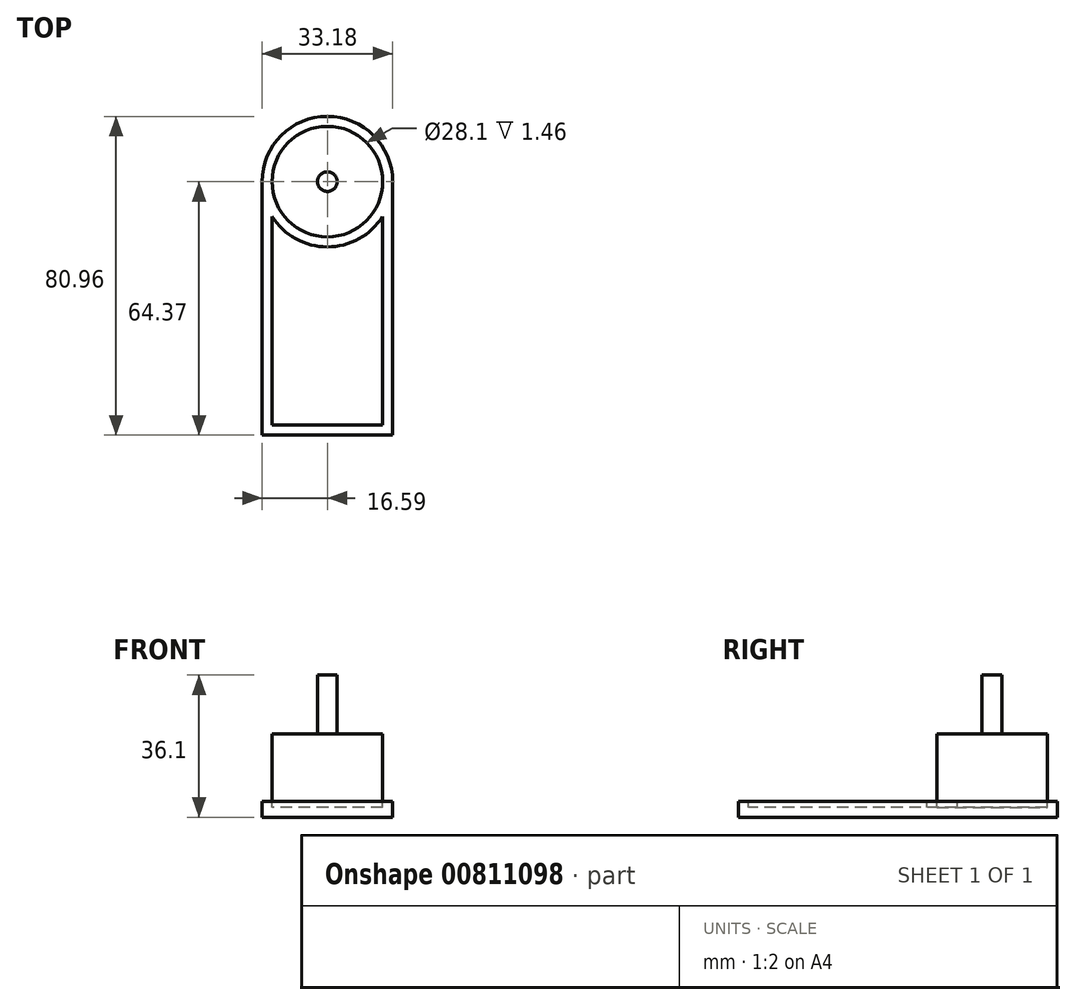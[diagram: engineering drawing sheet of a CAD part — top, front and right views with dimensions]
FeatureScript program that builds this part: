
annotation { "Feature Type Name" : "Feature", "Feature Type Description" : "" }
export const myFeature = defineFeature(function(context is Context, id is Id, definition is map)
    precondition{}
    {
        {
            var Q0;
            Q0=qCreatedBy(makeId("Top.planeOp"),FACE);
            var sketch = newSketch(context, id + "F0", { "sketchPlane" : qUnion([Q0])});
            skCircle(sketch, "E0", {"center": v(0, 0) * mm, "radius": 14.05 * mm});
            skSolve(sketch);
        }
        {
            var Q0;
            Q0=makeQuery(id+"F0.imprint","IMPRINT",FACE,{"disambiguationData":[TD([[makeQuery(id+"F0.imprint","IMPRINT",EDGE,{"derivedFrom":sQuery(id+"F0.wireOp",EDGE,"E0")}),1.0]])]});
            extrude(context, id + "F1", {"entities" : qUnion([Q0]), "depth" : 17.1 * mm, "offsetDistance" : 25.4 * mm});
        }
        {
            var Q0;
            Q0=makeQuery(id+"F1.opExtrude","CAP_FACE",FACE,{"disambiguationData":[OSD([sQuery(id+"F0.wireOp",EDGE,"E0")])],"isStart":false});
            var sketch = newSketch(context, id + "F2", { "sketchPlane" : qUnion([Q0])});
            skCircle(sketch, "E1", {"center": v(0, 0) * mm, "radius": 2.5 * mm});
            skSolve(sketch);
        }
        {
            var Q0;
            Q0=makeQuery(id+"F2.imprint","IMPRINT",FACE,{"disambiguationData":[TD([[makeQuery(id+"F2.imprint","IMPRINT",EDGE,{"derivedFrom":sQuery(id+"F2.wireOp",EDGE,"E1")}),1.0]])]});
            extrude(context, id + "F3", {"entities" : qUnion([Q0]), "operationType" : NewBodyOperationType.ADD, "depth" : 15 * mm, "offsetDistance" : 25.4 * mm});
        }
        {
            var Q0;
            Q0=makeQuery(id+"F1.opExtrude","CAP_FACE",FACE,{"disambiguationData":[OSD([sQuery(id+"F0.wireOp",EDGE,"E0")])],"isStart":true});
            var sketch = newSketch(context, id + "F4", { "sketchPlane" : qUnion([Q0])});
            skCircle(sketch, "E2.0", {"center": v(0, 0) * mm, "radius": 14.05 * mm, "construction": true});
            skCircle(sketch, "E3.0", {"center": v(0, 0) * mm, "radius": 16.59 * mm});
            skLineSegment(sketch, "E4.bottom", {"start": v(16.59, 0) * mm, "end": v(0, 0) * mm});
            skLineSegment(sketch, "E4.top", {"start": v(16.6, 64.37) * mm, "end": v(0, 64.37) * mm});
            skLineSegment(sketch, "E4.left", {"start": v(16.6, 0) * mm, "end": v(16.59, 64.37) * mm});
            skLineSegment(sketch, "E4.right", {"start": v(0, 0) * mm, "end": v(0, 64.37) * mm, "construction": true});
            skLineSegment(sketch, "E5.bottom", {"start": v(-16.59, 0) * mm, "end": v(0, 0) * mm});
            skLineSegment(sketch, "E5.top", {"start": v(-16.6, 64.37) * mm, "end": v(0, 64.37) * mm});
            skLineSegment(sketch, "E5.left", {"start": v(-16.59, 0) * mm, "end": v(-16.6, 64.37) * mm});
            skSolve(sketch);
        }
        {
            var Q0;
            Q0=makeQuery(id+"F4.imprint","IMPRINT",FACE,{"disambiguationData":[TD([[makeQuery(id+"F4.imprint","IMPRINT",EDGE,{"derivedFrom":sQuery(id+"F4.wireOp",EDGE,"E4.top")}),1.0]])]});
            var Q1;
            {var subQ0=sQuery(id+"F4.wireOp",EDGE,"E4.bottom");var subQ5=makeQuery(id+"F1.opExtrude","CAP_EDGE",EDGE,{"disambiguationData":[OSD([sQuery(id+"F0.wireOp",EDGE,"E0")])],"isStart":true});var subQ7=makeQuery(id+"F4.imprint","INTERSECT",VERTEX,{"derivedFrom":[subQ5,subQ0]});Q1=makeQuery(id+"F4.imprint","IMPRINT",FACE,{"disambiguationData":[TD([[makeQuery(id+"F4.imprint","IMPRINT",EDGE,{"disambiguationData":[TD([[subQ7,-1.0]])],"derivedFrom":subQ5}),1.0]])]});}
            var Q2;
            {var subQ0=sQuery(id+"F4.wireOp",EDGE,"E4.bottom");var subQ5=makeQuery(id+"F1.opExtrude","CAP_EDGE",EDGE,{"disambiguationData":[OSD([sQuery(id+"F0.wireOp",EDGE,"E0")])],"isStart":true});var subQ6=makeQuery(id+"F4.imprint","INTERSECT",VERTEX,{"derivedFrom":[subQ5,subQ0]});Q2=makeQuery(id+"F4.imprint","IMPRINT",FACE,{"disambiguationData":[TD([[makeQuery(id+"F4.imprint","IMPRINT",EDGE,{"disambiguationData":[TD([[subQ6,1.0]])],"derivedFrom":subQ5}),1.0]])]});}
            var Q3;
            {var subQ0=sQuery(id+"F4.wireOp",EDGE,"E5.bottom");var subQ1=sQuery(id+"F4.wireOp",EDGE,"E4.bottom");var subQ2=makeQuery(id+"F4.imprint","INTERSECT",VERTEX,{"derivedFrom":[subQ1,subQ0]});Q3=makeQuery(id+"F4.imprint","IMPRINT",FACE,{"disambiguationData":[TD([[makeQuery(id+"F4.imprint","IMPRINT",EDGE,{"disambiguationData":[TD([[subQ2,1.0]])],"derivedFrom":subQ1}),1.0]])]});}
            var Q4;
            {var subQ0=sQuery(id+"F4.wireOp",EDGE,"E5.bottom");var subQ1=sQuery(id+"F4.wireOp",EDGE,"E4.bottom");var subQ2=makeQuery(id+"F4.imprint","INTERSECT",VERTEX,{"derivedFrom":[subQ1,subQ0]});Q4=makeQuery(id+"F4.imprint","IMPRINT",FACE,{"disambiguationData":[TD([[makeQuery(id+"F4.imprint","IMPRINT",EDGE,{"disambiguationData":[TD([[subQ2,1.0]])],"derivedFrom":subQ1}),-1.0]])]});}
            extrude(context, id + "F5", {"entities" : qUnion([Q0, Q1, Q2, Q3, Q4]), "depth" : 4 * mm, "offsetDistance" : 25.4 * mm});
        }
        {
            var Q0;
            Q0=makeQuery(id+"F5.opExtrude","CAP_FACE",FACE,{"disambiguationData":[OSD([sQuery(id+"F4.wireOp",EDGE,"E3.0"),sQuery(id+"F4.wireOp",EDGE,"E4.top"),sQuery(id+"F4.wireOp",EDGE,"E4.left"),sQuery(id+"F4.wireOp",EDGE,"E5.top"),sQuery(id+"F4.wireOp",EDGE,"E5.left")])],"isStart":true});
            shell(context, id + "F6", {"entities" : qUnion([Q0]), "thickness" : 2.54 * mm});
        }
        {
            var Q0;
            {var subQ0=sQuery(id+"F4.wireOp",EDGE,"E4.bottom");var subQ5=makeQuery(id+"F1.opExtrude","CAP_EDGE",EDGE,{"disambiguationData":[OSD([sQuery(id+"F0.wireOp",EDGE,"E0")])],"isStart":true});var subQ6=makeQuery(id+"F4.imprint","INTERSECT",VERTEX,{"derivedFrom":[subQ5,subQ0]});Q0=makeQuery(id+"F4.imprint","IMPRINT",FACE,{"disambiguationData":[TD([[makeQuery(id+"F4.imprint","IMPRINT",EDGE,{"disambiguationData":[TD([[subQ6,1.0]])],"derivedFrom":subQ5}),1.0]])]});}
            extrude(context, id + "F7", {"entities" : qUnion([Q0]), "operationType" : NewBodyOperationType.ADD, "depth" : 2.54 * mm, "offsetDistance" : 25.4 * mm});
        }
    });
